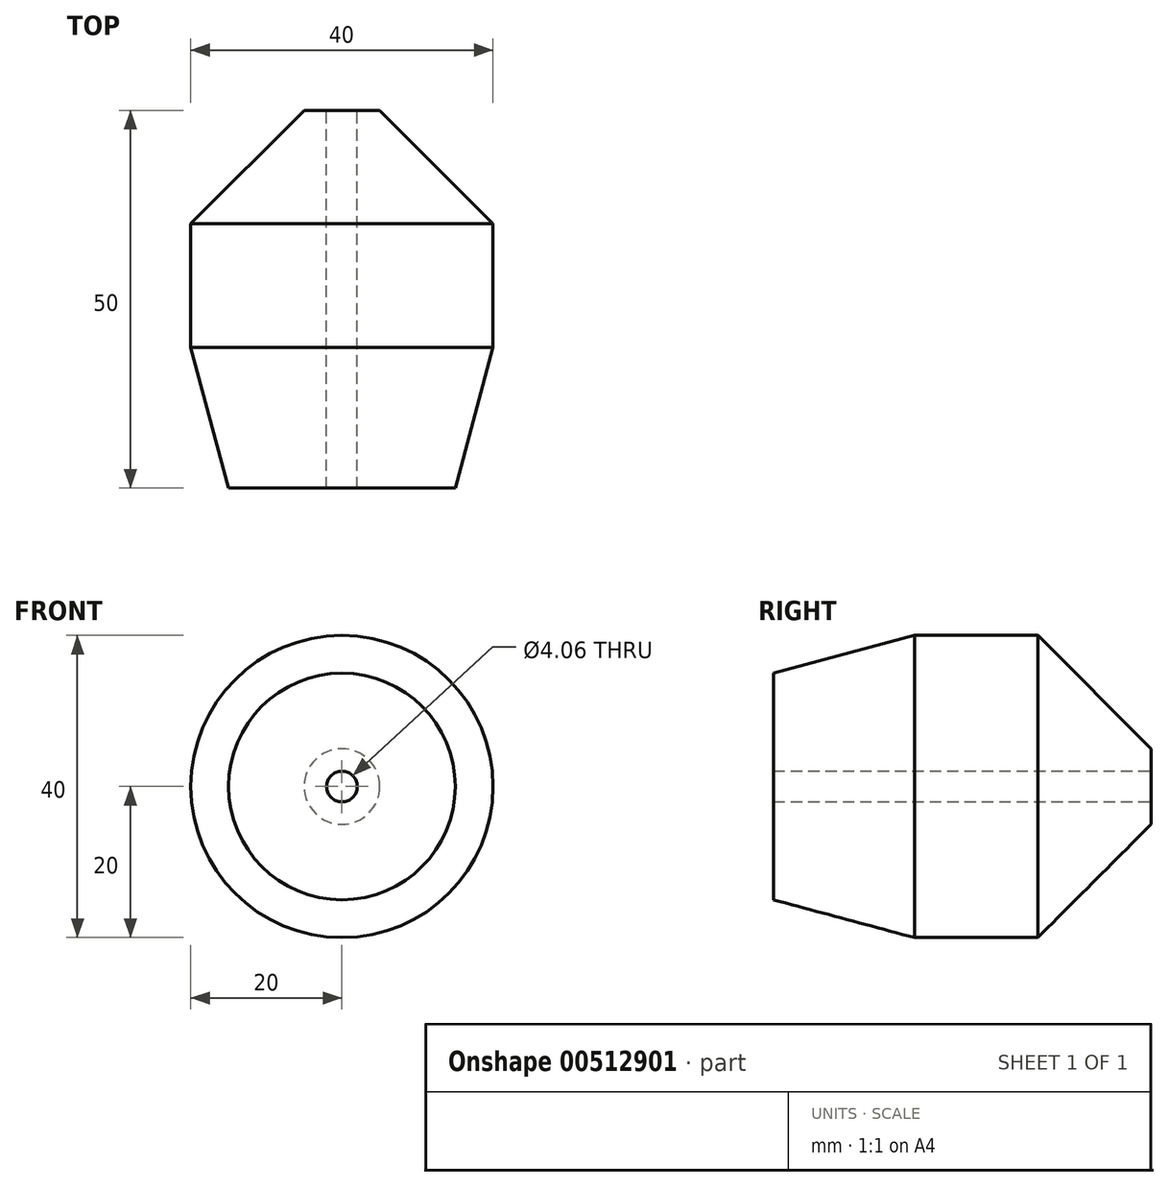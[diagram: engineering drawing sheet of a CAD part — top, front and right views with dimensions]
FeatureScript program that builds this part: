
annotation { "Feature Type Name" : "Feature", "Feature Type Description" : "" }
export const myFeature = defineFeature(function(context is Context, id is Id, definition is map)
    precondition{}
    {
        {
            var Q0;
            Q0=qCreatedBy(makeId("Front.planeOp"),FACE);
            var sketch = newSketch(context, id + "F0", { "sketchPlane" : qUnion([Q0])});
            skCircle(sketch, "E0", {"center": v(0, 0) * mm, "radius": 2.03 * mm});
            skCircle(sketch, "E1", {"center": v(0, 0) * mm, "radius": 20 * mm});
            skSolve(sketch);
        }
        {
            var Q0;
            Q0=makeQuery(id+"F0.imprint","IMPRINT",FACE,{"disambiguationData":[TD([[makeQuery(id+"F0.imprint","IMPRINT",EDGE,{"derivedFrom":sQuery(id+"F0.wireOp",EDGE,"E0")}),-1.0]])]});
            extrude(context, id + "F1", {"entities" : qUnion([Q0]), "depth" : 50 * mm, "offsetDistance" : 25 * mm});
        }
        {
            var Q0;
            Q0=makeQuery(id+"F1.opExtrude","CAP_EDGE",EDGE,{"disambiguationData":[OSD([sQuery(id+"F0.wireOp",EDGE,"E1")])],"isStart":false});
            chamfer(context, id + "F2", {"entities" : qUnion([Q0]), "chamferType" : ChamferType.OFFSET_ANGLE, "width" : 5 * mm, "oppositeDirection" : false, "angle" : 75 * degree, "tangentPropagation" : true});
        }
        {
            var Q0;
            Q0=makeQuery(id+"F1.opExtrude","CAP_EDGE",EDGE,{"disambiguationData":[OSD([sQuery(id+"F0.wireOp",EDGE,"E1")])],"isStart":true});
            chamfer(context, id + "F3", {"entities" : qUnion([Q0]), "width" : 15 * mm, "tangentPropagation" : true});
        }
    });
